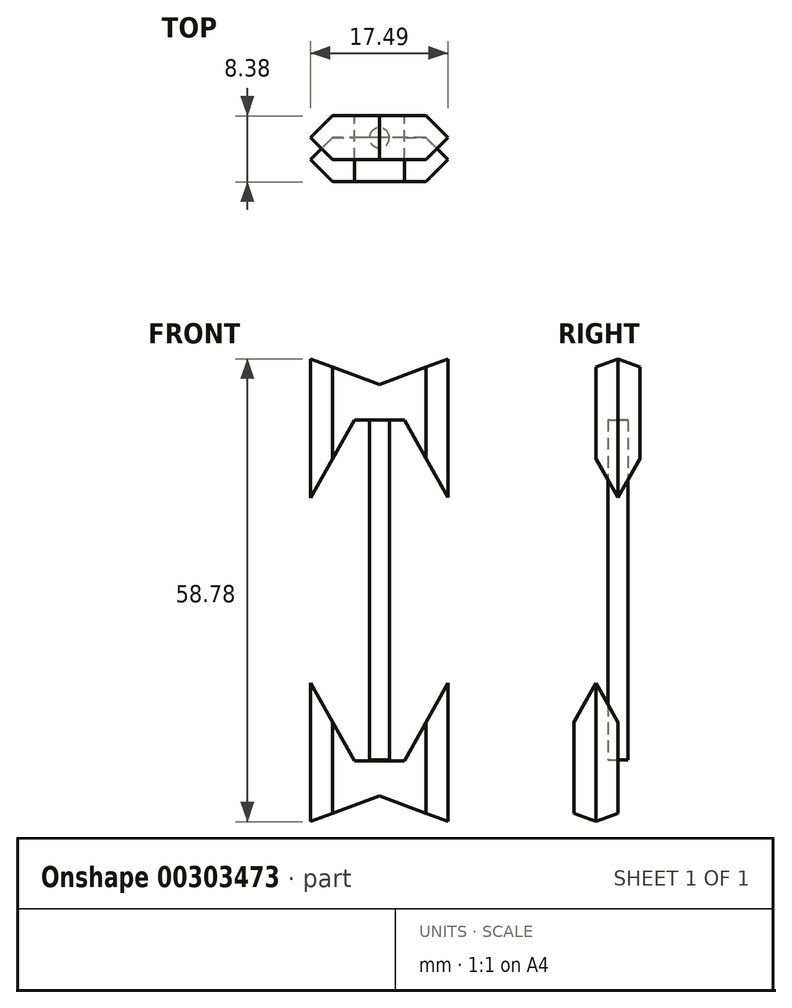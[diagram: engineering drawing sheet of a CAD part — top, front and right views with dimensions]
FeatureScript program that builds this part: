
annotation { "Feature Type Name" : "Feature", "Feature Type Description" : "" }
export const myFeature = defineFeature(function(context is Context, id is Id, definition is map)
    precondition{}
    {
        {
            var Q0;
            Q0=qCreatedBy(makeId("Top.planeOp"),FACE);
            var sketch = newSketch(context, id + "F0", { "sketchPlane" : qUnion([Q0])});
            skCircle(sketch, "E0", {"center": v(0, 0) * mm, "radius": 1.27 * mm});
            skSolve(sketch);
        }
        {
            var Q0;
            Q0=qSketchRegion(id+"F0",true);
            extrude(context, id + "F1", {"entities" : qUnion([Q0]), "depth" : 43.18 * mm});
        }
        {
            var Q0;
            Q0=qCreatedBy(makeId("Front.planeOp"),FACE);
            var sketch = newSketch(context, id + "F2", { "sketchPlane" : qUnion([Q0])});
            skLineSegment(sketch, "E1", {"start": v(3.17, 43.18) * mm, "end": v(11, 29.24) * mm});
            skLineSegment(sketch, "E2", {"start": v(11, 29.24) * mm, "end": v(11, 51.75) * mm});
            skLineSegment(sketch, "E3", {"start": v(11, 51.75) * mm, "end": v(0, 47.67) * mm});
            skLineSegment(sketch, "E4", {"start": v(0, 47.67) * mm, "end": v(-11.06, 51.75) * mm});
            skLineSegment(sketch, "E5", {"start": v(-11.06, 51.75) * mm, "end": v(-11.06, 29.24) * mm});
            skLineSegment(sketch, "E6", {"start": v(-11.06, 29.24) * mm, "end": v(-3.17, 43.18) * mm});
            skLineSegment(sketch, "E7", {"start": v(3.17, 43.18) * mm, "end": v(-3.17, 43.18) * mm});
            skLineSegment(sketch, "E8", {"start": v(25.06, 21.52) * mm, "end": v(-23.76, 21.52) * mm, "construction": true});
            skLineSegment(sketch, "E9.MirrorCS", {"start": v(3.17, -0.13) * mm, "end": v(11, 13.8) * mm});
            skLineSegment(sketch, "E10.MirrorCS", {"start": v(11, 13.8) * mm, "end": v(11, -8.7) * mm});
            skLineSegment(sketch, "E11.MirrorCS", {"start": v(11, -8.7) * mm, "end": v(0, -4.63) * mm});
            skLineSegment(sketch, "E12.MirrorCS", {"start": v(0, -4.63) * mm, "end": v(-11.06, -8.7) * mm});
            skLineSegment(sketch, "E13.MirrorCS", {"start": v(-11.06, -8.7) * mm, "end": v(-11.06, 13.8) * mm});
            skLineSegment(sketch, "E14.MirrorCS", {"start": v(-11.06, 13.8) * mm, "end": v(-3.17, -0.13) * mm});
            skLineSegment(sketch, "E15.MirrorCS", {"start": v(3.17, -0.13) * mm, "end": v(-3.17, -0.13) * mm});
            skSolve(sketch);
        }
        {
            var Q0;
            Q0=makeQuery(id+"F2.imprint","IMPRINT",FACE,{"disambiguationData":[TD([[makeQuery(id+"F2.imprint","IMPRINT",EDGE,{"derivedFrom":sQuery(id+"F2.wireOp",EDGE,"E1")}),1.0]])]});
            extrude(context, id + "F3", {"entities" : qUnion([Q0]), "endBound" : BoundingType.SYMMETRIC, "depth" : 5.6 * mm});
        }
        {
            var Q0;
            Q0=makeQuery(id+"F3.opExtrude","CAP_EDGE",EDGE,{"disambiguationData":[OSD([sQuery(id+"F2.wireOp",EDGE,"E2")])],"isStart":false});
            var Q1;
            Q1=makeQuery(id+"F3.opExtrude","CAP_EDGE",EDGE,{"disambiguationData":[OSD([sQuery(id+"F2.wireOp",EDGE,"E2")])],"isStart":true});
            var Q2;
            Q2=makeQuery(id+"F3.opExtrude","CAP_EDGE",EDGE,{"disambiguationData":[OSD([sQuery(id+"F2.wireOp",EDGE,"E5")])],"isStart":false});
            var Q3;
            Q3=makeQuery(id+"F3.opExtrude","CAP_EDGE",EDGE,{"disambiguationData":[OSD([sQuery(id+"F2.wireOp",EDGE,"E5")])],"isStart":true});
            chamfer(context, id + "F4", {"entities" : qUnion([Q0, Q1, Q2, Q3]), "width" : 5.08 * mm, "tangentPropagation" : true});
        }
        {
            var Q0;
            Q0=makeQuery(id+"F2.imprint","IMPRINT",FACE,{"disambiguationData":[TD([[makeQuery(id+"F2.imprint","IMPRINT",EDGE,{"derivedFrom":sQuery(id+"F2.wireOp",EDGE,"E9.MirrorCS")}),-1.0]])]});
            extrude(context, id + "F5", {"entities" : qUnion([Q0]), "depth" : 5.6 * mm});
        }
        {
            var Q0;
            Q0=makeQuery(id+"F5.opExtrude","CAP_EDGE",EDGE,{"disambiguationData":[OSD([sQuery(id+"F2.wireOp",EDGE,"E13.MirrorCS")])],"isStart":true});
            var Q1;
            Q1=makeQuery(id+"F5.opExtrude","CAP_EDGE",EDGE,{"disambiguationData":[OSD([sQuery(id+"F2.wireOp",EDGE,"E13.MirrorCS")])],"isStart":false});
            var Q2;
            Q2=makeQuery(id+"F5.opExtrude","CAP_EDGE",EDGE,{"disambiguationData":[OSD([sQuery(id+"F2.wireOp",EDGE,"E10.MirrorCS")])],"isStart":false});
            var Q3;
            Q3=makeQuery(id+"F5.opExtrude","CAP_EDGE",EDGE,{"disambiguationData":[OSD([sQuery(id+"F2.wireOp",EDGE,"E10.MirrorCS")])],"isStart":true});
            chamfer(context, id + "F6", {"entities" : qUnion([Q0, Q1, Q2, Q3]), "width" : 5.08 * mm, "tangentPropagation" : true});
        }
    });
